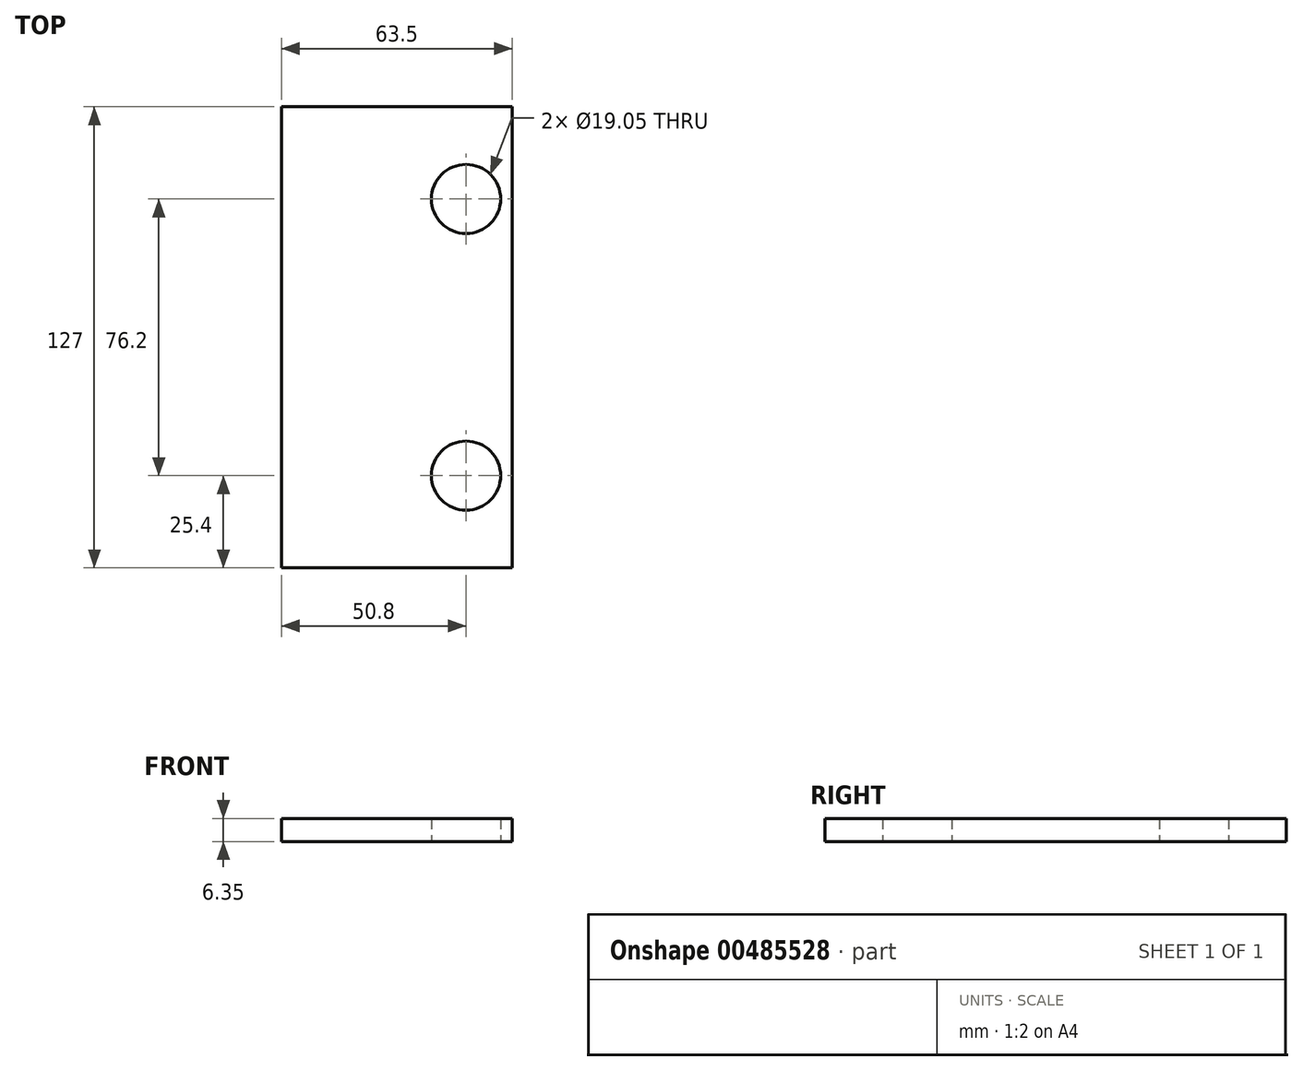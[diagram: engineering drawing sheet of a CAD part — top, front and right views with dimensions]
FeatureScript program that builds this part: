
annotation { "Feature Type Name" : "Feature", "Feature Type Description" : "" }
export const myFeature = defineFeature(function(context is Context, id is Id, definition is map)
    precondition{}
    {
        {
            var Q0;
            Q0=qCreatedBy(makeId("Top.planeOp"),FACE);
            var sketch = newSketch(context, id + "F0", { "sketchPlane" : qUnion([Q0])});
            skLineSegment(sketch, "E0.bottom", {"start": v(31.75, 63.5) * mm, "end": v(-31.75, 63.5) * mm});
            skLineSegment(sketch, "E0.top", {"start": v(31.75, -63.5) * mm, "end": v(-31.75, -63.5) * mm});
            skLineSegment(sketch, "E0.left", {"start": v(31.75, 63.5) * mm, "end": v(31.75, -63.5) * mm});
            skLineSegment(sketch, "E0.right", {"start": v(-31.75, 63.5) * mm, "end": v(-31.75, -63.5) * mm});
            skPoint(sketch, "E0.middle", {"position": v(0, 0) * mm});
            skCircle(sketch, "E1", {"center": v(19.05, -38.1) * mm, "radius": 9.53 * mm});
            skCircle(sketch, "E2", {"center": v(19.05, 38.1) * mm, "radius": 9.53 * mm});
            skSolve(sketch);
        }
        {
            var Q0;
            Q0 = qSketchRegion(id + "F0", true);
            extrude(context, id + "F1", {"entities" : qUnion([Q0]), "depth" : 6.35 * mm});
        }
    });
